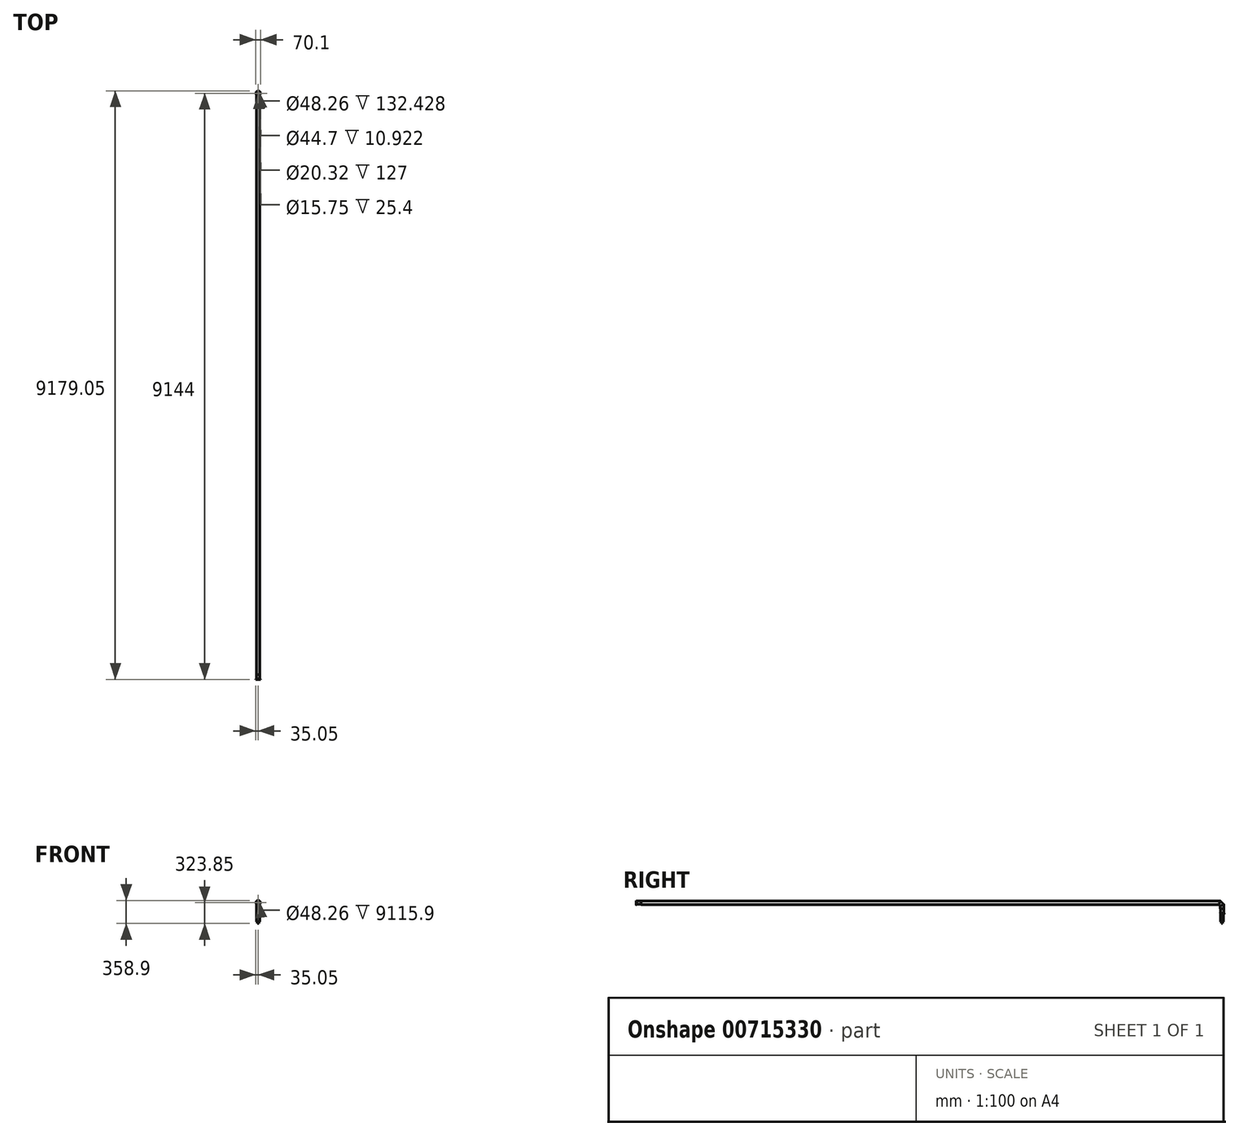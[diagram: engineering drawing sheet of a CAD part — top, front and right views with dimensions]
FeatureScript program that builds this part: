
annotation { "Feature Type Name" : "Feature", "Feature Type Description" : "" }
export const myFeature = defineFeature(function(context is Context, id is Id, definition is map)
    precondition{}
    {
        {
            var Q0;
            Q0=qCreatedBy(makeId("Front.planeOp"),FACE);
            var sketch = newSketch(context, id + "F0", { "sketchPlane" : qUnion([Q0])});
            skCircle(sketch, "E0", {"center": v(0, 0) * mm, "radius": 22.23 * mm, "construction": true});
            skSolve(sketch);
        }
        {
            var Q0;
            Q0=qCreatedBy(makeId("Front.planeOp"),FACE);
            var sketch = newSketch(context, id + "F1", { "sketchPlane" : qUnion([Q0])});
            skCircle(sketch, "E1", {"center": v(0, 0) * mm, "radius": 24.13 * mm});
            skCircle(sketch, "E2", {"center": v(0, 0) * mm, "radius": 35.05 * mm});
            skSolve(sketch);
        }
        {
            var Q0;
            Q0 = qSketchRegion(id + "F1", true);
            extrude(context, id + "F2", {"entities" : qUnion([Q0]), "oppositeDirection" : true, "depth" : 5.84 * mm, "offsetDistance" : 25.4 * mm});
        }
        {
            var Q0;
            Q0=makeQuery(id+"F2.opExtrude","CAP_EDGE",EDGE,{"disambiguationData":[OSD([sQuery(id+"F1.wireOp",EDGE,"E2")])],"isStart":false});
            chamfer(context, id + "F3", {"entities" : qUnion([Q0]), "chamferType" : ChamferType.OFFSET_ANGLE, "width" : 2.54 * mm, "oppositeDirection" : false, "angle" : 70 * degree, "tangentPropagation" : true});
        }
        {
            var Q0;
            Q0=makeQuery(id+"F2.opExtrude","CAP_FACE",FACE,{"disambiguationData":[OSD([sQuery(id+"F1.wireOp",EDGE,"E1"),sQuery(id+"F1.wireOp",EDGE,"E2")])],"isStart":false});
            var sketch = newSketch(context, id + "F4", { "sketchPlane" : qUnion([Q0])});
            skCircle(sketch, "E3", {"center": v(0, 0) * mm, "radius": 28.07 * mm});
            skCircle(sketch, "E4", {"center": v(0, 0) * mm, "radius": 24.13 * mm});
            skSolve(sketch);
        }
        {
            var Q0;
            Q0 = qSketchRegion(id + "F4", true);
            extrude(context, id + "F5", {"entities" : qUnion([Q0]), "operationType" : NewBodyOperationType.ADD, "depth" : 2.54 * mm, "offsetDistance" : 25.4 * mm});
        }
        {
            var Q0;
            Q0=makeQuery(id+"F5.opExtrude","CAP_FACE",FACE,{"disambiguationData":[OSD([sQuery(id+"F4.wireOp",EDGE,"E3"),sQuery(id+"F4.wireOp",EDGE,"E4")])],"isStart":false});
            var sketch = newSketch(context, id + "F6", { "sketchPlane" : qUnion([Q0])});
            skCircle(sketch, "E5", {"center": v(0, 0) * mm, "radius": 26.55 * mm});
            skCircle(sketch, "E6", {"center": v(0, 0) * mm, "radius": 24.13 * mm});
            skSolve(sketch);
        }
        {
            var Q0;
            Q0 = qSketchRegion(id + "F6", true);
            extrude(context, id + "F7", {"entities" : qUnion([Q0]), "operationType" : NewBodyOperationType.ADD, "depth" : 2.54 * mm, "offsetDistance" : 25.4 * mm});
        }
        {
            var Q0;
            Q0=makeQuery(id+"F7.opExtrude","CAP_FACE",FACE,{"disambiguationData":[OSD([sQuery(id+"F6.wireOp",EDGE,"E5"),sQuery(id+"F6.wireOp",EDGE,"E6")])],"isStart":false});
            var sketch = newSketch(context, id + "F8", { "sketchPlane" : qUnion([Q0])});
            skCircle(sketch, "E7", {"center": v(0, 0) * mm, "radius": 24.13 * mm});
            skCircle(sketch, "E8", {"center": v(0, 0) * mm, "radius": 25.4 * mm});
            skSolve(sketch);
        }
        {
            var Q0;
            Q0 = qSketchRegion(id + "F8", true);
            extrude(context, id + "F9", {"entities" : qUnion([Q0]), "operationType" : NewBodyOperationType.ADD, "depth" : 65.28 * mm, "offsetDistance" : 25.4 * mm});
        }
        {
            var Q0;
            Q0=makeQuery(id+"F9.opExtrude","CAP_FACE",FACE,{"disambiguationData":[OSD([sQuery(id+"F8.wireOp",EDGE,"E7"),sQuery(id+"F8.wireOp",EDGE,"E8")])],"isStart":false});
            var sketch = newSketch(context, id + "F10", { "sketchPlane" : qUnion([Q0])});
            skCircle(sketch, "E9", {"center": v(0, 0) * mm, "radius": 27.94 * mm});
            skCircle(sketch, "E10", {"center": v(0, 0) * mm, "radius": 24.13 * mm});
            skSolve(sketch);
        }
        {
            var Q0;
            Q0=qCreatedBy(makeId("Right.planeOp"),FACE);
            var sketch = newSketch(context, id + "F11", { "sketchPlane" : qUnion([Q0])});
            skLineSegment(sketch, "E11", {"start": v(0, 0) * mm, "end": v(9144, 0) * mm, "construction": true});
            skLineSegment(sketch, "E12", {"start": v(9144, 0) * mm, "end": v(9144, -95.25) * mm, "construction": true});
            skLineSegment(sketch, "E13", {"start": v(9105.9, 0) * mm, "end": v(9144, -38.1) * mm});
            skLineSegment(sketch, "E14", {"start": v(9144, -38.1) * mm, "end": v(9144, -95.25) * mm});
            skLineSegment(sketch, "E15", {"start": v(76.2, 0) * mm, "end": v(9105.9, 0) * mm});
            skSolve(sketch);
        }
        {
            var Q0;
            Q0 = qSketchRegion(id + "F10", true);
            var Q1;
            Q1 = qConstructionFilter(qBodyType(qCreatedBy(id + "F11" ,EDGE), BodyType.WIRE), ConstructionObject.NO);
            sweep(context, id + "F12", {"operationType" : NewBodyOperationType.ADD, "profiles" : qUnion([Q0]), "path" : qUnion([Q1])});
        }
        {
            var Q0;
            Q0=makeQuery(id+"F12.opSweep","CAP_EDGE",EDGE,{"disambiguationData":[OSD([sQuery(id+"F10.wireOp",EDGE,"E9"),sQuery(id+"F11.wireOp",VERTEX,"E15.start")])],"isStart":true});
            fillet(context, id + "F13", {"entities" : qUnion([Q0]), "radius" : 1.27 * mm, "tangentPropagation" : true, "allowEdgeOverflow" : false});
        }
        {
            var Q0;
            Q0=makeQuery(id+"F12.opSweep","CAP_FACE",FACE,{"disambiguationData":[OSD([sQuery(id+"F10.wireOp",EDGE,"E9"),sQuery(id+"F10.wireOp",EDGE,"E10"),sQuery(id+"F11.wireOp",VERTEX,"E14.end")])],"isStart":false});
            var sketch = newSketch(context, id + "F14", { "sketchPlane" : qUnion([Q0])});
            skCircle(sketch, "E16", {"center": v(0, -9144) * mm, "radius": 24.13 * mm});
            skCircle(sketch, "E17", {"center": v(0, -9144) * mm, "radius": 25.4 * mm});
            skSolve(sketch);
        }
        {
            var Q0;
            Q0=makeQuery(id+"F12.opSweep","CAP_EDGE",EDGE,{"disambiguationData":[OSD([sQuery(id+"F10.wireOp",EDGE,"E9"),sQuery(id+"F11.wireOp",VERTEX,"E14.end")])],"isStart":false});
            fillet(context, id + "F15", {"entities" : qUnion([Q0]), "radius" : 1.27 * mm, "tangentPropagation" : true, "allowEdgeOverflow" : false});
        }
        {
            var Q0;
            Q0 = qSketchRegion(id + "F14", true);
            extrude(context, id + "F16", {"entities" : qUnion([Q0]), "operationType" : NewBodyOperationType.ADD, "depth" : 76.2 * mm, "offsetDistance" : 25.4 * mm});
        }
        {
            var Q0;
            Q0=makeQuery(id+"F16.opExtrude","CAP_FACE",FACE,{"disambiguationData":[OSD([sQuery(id+"F14.wireOp",EDGE,"E16"),sQuery(id+"F14.wireOp",EDGE,"E17")])],"isStart":false});
            var sketch = newSketch(context, id + "F17", { "sketchPlane" : qUnion([Q0])});
            skCircle(sketch, "E18", {"center": v(0, -9144) * mm, "radius": 35.05 * mm});
            skCircle(sketch, "E19", {"center": v(0, -9144) * mm, "radius": 22.35 * mm});
            skSolve(sketch);
        }
        {
            var Q0;
            Q0 = qSketchRegion(id + "F17", true);
            extrude(context, id + "F18", {"entities" : qUnion([Q0]), "operationType" : NewBodyOperationType.ADD, "oppositeDirection" : true, "depth" : 5.84 * mm, "offsetDistance" : 25.4 * mm});
        }
        {
            var Q0;
            Q0=makeQuery(id+"F18.opExtrude","CAP_EDGE",EDGE,{"disambiguationData":[OSD([sQuery(id+"F17.wireOp",EDGE,"E18")])],"isStart":false});
            chamfer(context, id + "F19", {"entities" : qUnion([Q0]), "chamferType" : ChamferType.OFFSET_ANGLE, "width" : 2.54 * mm, "oppositeDirection" : false, "angle" : 70 * degree, "tangentPropagation" : true});
        }
        {
            var Q0;
            Q0=makeQuery(id+"F18.opExtrude","CAP_FACE",FACE,{"disambiguationData":[OSD([sQuery(id+"F17.wireOp",EDGE,"E18"),sQuery(id+"F17.wireOp",EDGE,"E19")])],"isStart":false});
            var sketch = newSketch(context, id + "F20", { "sketchPlane" : qUnion([Q0])});
            skCircle(sketch, "E20", {"center": v(0, 9144) * mm, "radius": 22.35 * mm});
            skCircle(sketch, "E21", {"center": v(0, 9144) * mm, "radius": 28.07 * mm});
            skSolve(sketch);
        }
        {
            var Q0;
            Q0 = qSketchRegion(id + "F20", true);
            extrude(context, id + "F21", {"entities" : qUnion([Q0]), "operationType" : NewBodyOperationType.ADD, "depth" : 2.54 * mm, "offsetDistance" : 25.4 * mm});
        }
        {
            var Q0;
            Q0=makeQuery(id+"F21.opExtrude","CAP_FACE",FACE,{"disambiguationData":[OSD([sQuery(id+"F20.wireOp",EDGE,"E20"),sQuery(id+"F20.wireOp",EDGE,"E21")])],"isStart":false});
            var sketch = newSketch(context, id + "F22", { "sketchPlane" : qUnion([Q0])});
            skCircle(sketch, "E22", {"center": v(0, 9144) * mm, "radius": 22.35 * mm});
            skCircle(sketch, "E23", {"center": v(0, 9144) * mm, "radius": 26.8 * mm});
            skSolve(sketch);
        }
        {
            var Q0;
            Q0 = qSketchRegion(id + "F22", true);
            extrude(context, id + "F23", {"entities" : qUnion([Q0]), "operationType" : NewBodyOperationType.ADD, "depth" : 2.54 * mm, "offsetDistance" : 25.4 * mm});
        }
        {
            var Q0;
            Q0=makeQuery(id+"F18.boolean.opBoolean","MERGE",FACE,{"derivedFrom":[makeQuery(id+"F16.opExtrude","CAP_FACE",FACE,{"disambiguationData":[OSD([sQuery(id+"F14.wireOp",EDGE,"E16"),sQuery(id+"F14.wireOp",EDGE,"E17")])],"isStart":false}),makeQuery(id+"F18.opExtrude","CAP_FACE",FACE,{"disambiguationData":[OSD([sQuery(id+"F17.wireOp",EDGE,"E18"),sQuery(id+"F17.wireOp",EDGE,"E19")])],"isStart":true})]});
            var sketch = newSketch(context, id + "F24", { "sketchPlane" : qUnion([Q0])});
            skCircle(sketch, "E24", {"center": v(0, -9144) * mm, "radius": 10.16 * mm});
            skCircle(sketch, "E25", {"center": v(0, -9144) * mm, "radius": 24.13 * mm});
            skSolve(sketch);
        }
        {
            var Q0;
            Q0 = qSketchRegion(id + "F24", true);
            extrude(context, id + "F25", {"entities" : qUnion([Q0]), "operationType" : NewBodyOperationType.ADD, "depth" : 127 * mm, "offsetDistance" : 25.4 * mm});
        }
        {
            var Q0;
            Q0=makeQuery(id+"F25.opExtrude","CAP_FACE",FACE,{"disambiguationData":[OSD([sQuery(id+"F24.wireOp",EDGE,"E24"),sQuery(id+"F24.wireOp",EDGE,"E25")])],"isStart":false});
            var sketch = newSketch(context, id + "F26", { "sketchPlane" : qUnion([Q0])});
            skCircle(sketch, "E26", {"center": v(0, -9144) * mm, "radius": 10.67 * mm});
            skCircle(sketch, "E27", {"center": v(0, -9144) * mm, "radius": 7.87 * mm});
            skSolve(sketch);
        }
        {
            var Q0;
            Q0 = qSketchRegion(id + "F26", true);
            extrude(context, id + "F27", {"entities" : qUnion([Q0]), "operationType" : NewBodyOperationType.ADD, "depth" : 25.4 * mm, "offsetDistance" : 25.4 * mm});
        }
    });
